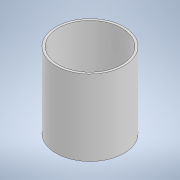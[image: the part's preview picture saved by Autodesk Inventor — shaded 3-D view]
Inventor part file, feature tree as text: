
AUTODESK INVENTOR PART (.ipt)
format: ipt  version: 2020 (Build 240168000, 168)  size: 99,840 bytes
history: native  units: in
note: dims shown in document units (in); Inventor stores cm internally (conversion verified against a paired STEP export)
features: revolve x1, sketch x1
ambient origin geometry x8: Origin, YZ Plane, XZ Plane, XY Plane, X Axis, Y Axis, Z Axis, Center Point
bodies: Solid1 (feature_tree)
feature tree (2):
  revolve  "Revolution1"  [1 undecoded]
  sketch  "Sketch1"  dims[d1=0.1181in d8=1.6535in d10=0.3937in d11=3.5521in d12=90.0deg]
note: 1 required parameter value undecoded (feature->parameter linkage not recoverable at this tier; creation-order binding heuristic only, values carry confidence <= 0.55)
